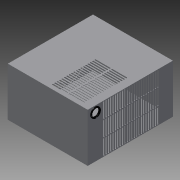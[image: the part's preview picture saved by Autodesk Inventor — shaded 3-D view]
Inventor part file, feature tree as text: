
AUTODESK INVENTOR PART (.ipt)
format: ipt  version: 2014 SP1 (Build 180222100, 222)  size: 1,281,536 bytes
history: native  units: in
note: dims shown in document units (in); Inventor stores cm internally (conversion verified against a paired STEP export)
features: extrude x9, sketch x9
ambient origin geometry x8: Origin, YZ Plane, XZ Plane, XY Plane, X Axis, Y Axis, Z Axis, Center Point
bodies: Solid1 (feature_tree)
feature tree (18):
  extrude  "Extrusion1"  Depth=5.925in
  extrude  "Extrusion2"  Depth=0.085in
  extrude  "Extrusion3"  Depth=2.823in
  extrude  "Extrusion4"  Depth=0.163in
  extrude  "Extrusion5"  Depth=0.163in
  extrude  "Extrusion6"  Depth=0.163in
  extrude  "Extrusion7"  Depth=0.1in TaperAngle=0.0deg
  extrude  "Extrusion8"  Depth=5.474in
  extrude  "Extrusion9"  Depth=5.839in
  sketch  "Sketch1"  dims[d0=5.56in d1=5.925in]
  sketch  "Sketch2"  dims[d2=3.38in d3=0.0in d4=0.085in]
  sketch  "Sketch4"  dims[d5=0.99in d6=2.823in]
  sketch  "Sketch5"  dims[d7=0.319in d8=0.99in d9=0.163in]
  sketch  "Sketch6"  dims[d10=0.085in d11=0.99in d12=0.99in d13=0.163in d14=0.163in d15=0.99in d16=0.163in]
  sketch  "Sketch8"  dims[d17=0.085in d18=0.99in d19=0.99in d20=0.163in d21=0.085in d22=0.99in d23=0.99in d24=0.163in d25=0.163in d26=0.99in d27=0.163in]
  sketch  "Sketch9"  dims[d28=0.085in d29=0.99in d30=0.99in d31=0.163in d32=0.085in d33=0.99in d34=0.99in d35=0.163in d36=0.163in d37=0.99in d38=0.163in]
  sketch  "Sketch10"  dims[d39=0.085in d40=0.99in d41=0.99in d42=0.163in d43=0.085in d44=0.99in d45=0.99in d46=0.163in d47=0.163in d50=0.163in d51=0.163in]
  sketch  "Sketch11"  dims[d52=0.085in d53=0.99in d54=0.99in d55=0.163in d56=0.085in d57=0.99in d58=0.99in d59=0.163in d60=0.163in d61=0.99in d62=0.163in d63=0.085in d64=0.99in d65=0.99in d66=0.163in d67=0.085in d68=0.99in d69=0.99in d70=0.163in d71=0.163in d72=0.99in d73=0.163in d74=0.085in d75=0.99in d76=0.99in d77=0.163in d78=0.085in d79=0.99in d80=0.99in d81=0.163in d82=0.163in d83=0.99in d84=0.163in d85=0.085in d86=0.99in d87=0.99in d88=0.163in d89=0.085in d90=0.99in d91=0.99in d92=0.163in d93=0.163in d94=0.163in d95=0.163in d96=0.1697in d97=20.0in d98=0.0in d102=5.474in d103=5.839in d104=0.043in d105=0.043in d106=3.35in d107=0.0in d108=0.043in d109=0.0in d223=0.99in d226=0.99in d230=0.99in d234=0.99in d235=0.99in d236=0.163in d237=0.99in d238=0.99in d239=0.163in d240=0.0in d241=0.99in d242=0.99in d243=0.163in d244=0.12in d245=0.12in d248=0.163in d249=0.99in d250=0.99in d251=0.163in d252=0.99in d253=0.99in d254=0.163in d255=0.0in d256=0.99in d257=0.99in d258=0.163in d259=0.12in d260=0.12in d261=0.99in d262=0.99in d263=0.163in d264=0.99in d265=0.99in d266=0.163in d267=0.0in d268=0.99in d269=0.99in d270=0.163in d271=0.12in d272=0.12in d273=0.99in d274=0.99in d275=0.163in d276=0.99in d277=0.99in d278=0.163in d279=0.0in d280=0.99in d281=0.99in d282=0.163in d283=0.12in d284=0.12in d285=0.99in d286=0.99in d287=0.163in d288=0.99in d289=0.99in d290=0.163in d291=0.0in d292=0.99in d293=0.99in d294=0.163in d295=0.12in d296=0.12in d297=0.163in d298=0.163in d299=0.163in d300=0.163in d301=0.99in d302=0.99in d303=0.163in d304=0.99in d305=0.99in d306=0.163in d307=0.0in d308=0.99in d309=0.99in d310=0.163in d311=0.12in d312=0.12in d313=0.99in d314=0.99in d315=0.163in d316=0.99in d317=0.99in d318=0.163in d319=0.0in d320=0.99in d321=0.99in d322=0.163in d323=0.12in d324=0.12in d325=0.99in d326=0.99in d327=0.163in d328=0.99in d329=0.99in d330=0.163in d331=0.0in d332=0.99in d333=0.99in d334=0.163in d335=0.12in d336=0.12in d337=0.99in d338=0.99in d339=0.163in d340=0.99in d341=0.99in d342=0.163in d343=0.0in d344=0.99in d345=0.99in d346=0.163in d347=0.12in d348=0.12in d349=0.163in d350=0.163in d351=0.163in d352=0.99in d353=0.99in d354=0.163in d355=0.99in d356=0.99in d357=0.163in d358=0.0in d359=0.99in d360=0.99in d361=0.163in d362=0.12in d363=0.12in d364=0.99in d365=0.99in d366=0.163in d367=0.99in d368=0.99in d369=0.163in d370=0.0in d371=0.99in d372=0.99in d373=0.163in d374=0.12in d375=0.12in d376=0.99in d379=0.99in d382=0.0in d383=0.99in d386=0.12in d387=0.12in d400=0.163in d401=0.163in d403=0.163in d404=0.163in d417=2.0in d418=0.0in d435=2.3622in d437=360.0deg d439=1.5748in d441=360.0deg d443=1.0in d444=0.0in d445=0.05in d446=0.0in d447=1.0in d448=0.0in d449=1.0in d450=0.5in d451=0.27in d452=0.1in d453=0.0in]
